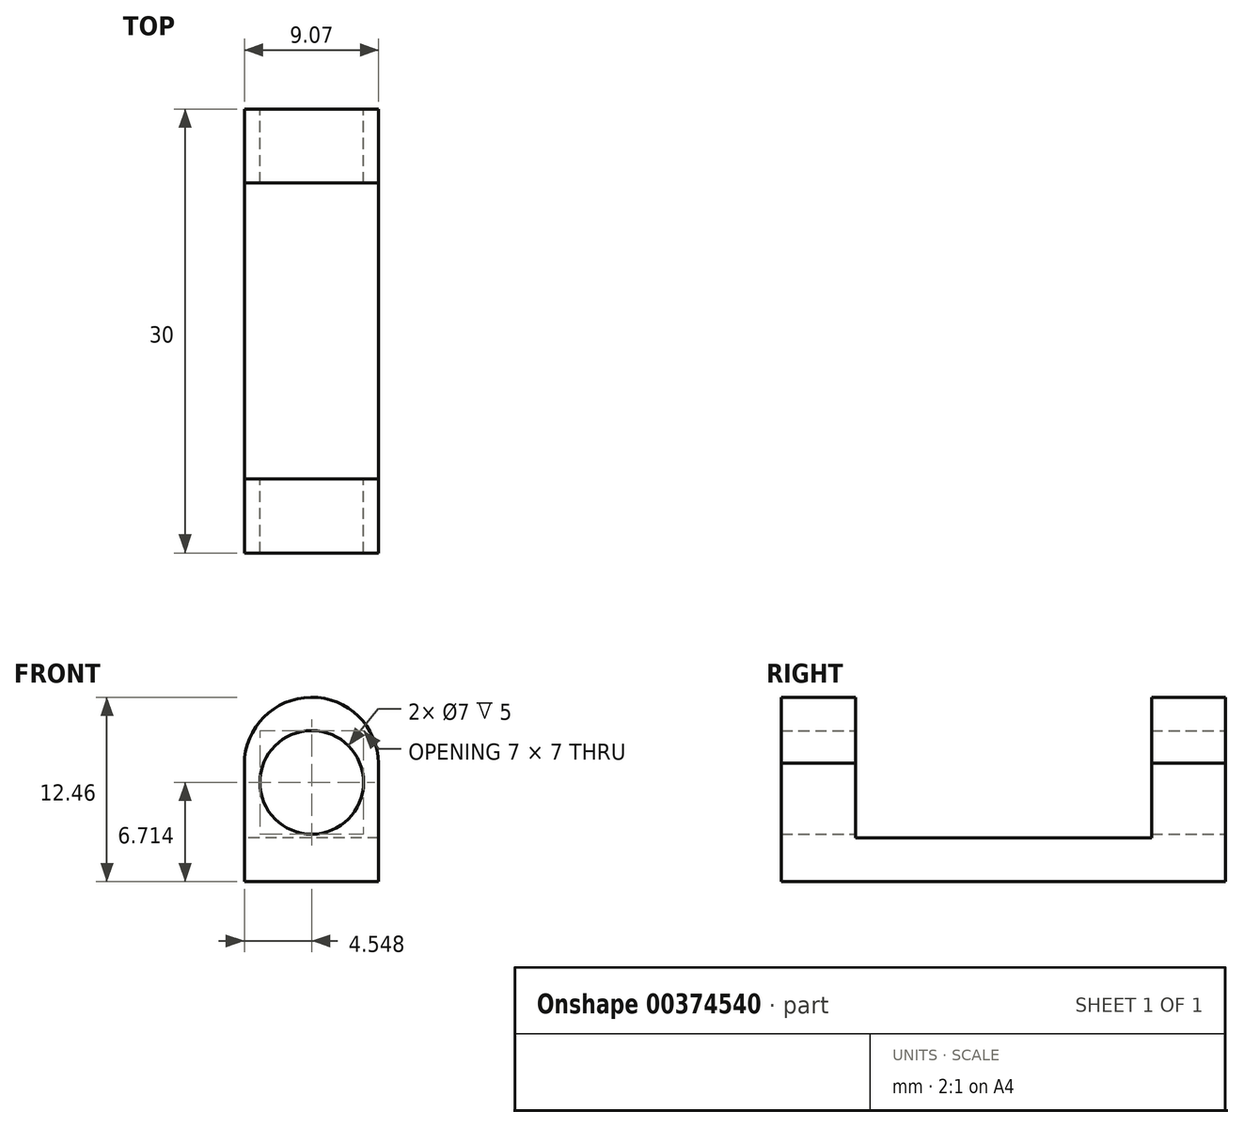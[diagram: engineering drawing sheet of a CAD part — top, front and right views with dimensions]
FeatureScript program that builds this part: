
annotation { "Feature Type Name" : "Feature", "Feature Type Description" : "" }
export const myFeature = defineFeature(function(context is Context, id is Id, definition is map)
    precondition{}
    {
        {
            var Q0;
            Q0=qCreatedBy(makeId("Front.planeOp"),FACE);
            var sketch = newSketch(context, id + "F0", { "sketchPlane" : qUnion([Q0])});
            skLineSegment(sketch, "E0", {"start": v(0, 0) * mm, "end": v(9.07, 0) * mm});
            skLineSegment(sketch, "E1", {"start": v(9.07, 0) * mm, "end": v(9.07, 8) * mm});
            skLineSegment(sketch, "E2", {"start": v(0, 0) * mm, "end": v(0, 7.93) * mm});
            skArc(sketch, "E3", {"start": v(9.07, 8) * mm, "mid": v(4.5, 12.46) * mm, "end": v(0, 7.93) * mm});
            skSolve(sketch);
        }
        {
            var Q0;
            Q0 = qSketchRegion(id + "F0", true);
            extrude(context, id + "F1", {"entities" : qUnion([Q0]), "depth" : 30 * mm});
        }
        {
            var Q0;
            Q0=qCreatedBy(makeId("Front.planeOp"),FACE);
            var sketch = newSketch(context, id + "F2", { "sketchPlane" : qUnion([Q0])});
            skCircle(sketch, "E4", {"center": v(4.55, 6.71) * mm, "radius": 3.5 * mm});
            skSolve(sketch);
        }
        {
            var Q0;
            Q0 = qSketchRegion(id + "F2", true);
            extrude(context, id + "F3", {"entities" : qUnion([Q0]), "operationType" : NewBodyOperationType.REMOVE, "endBound" : BoundingType.THROUGH_ALL, "depth" : 25 * mm});
        }
        {
            var Q0;
            Q0=qCreatedBy(makeId("Right.planeOp"),FACE);
            var sketch = newSketch(context, id + "F4", { "sketchPlane" : qUnion([Q0])});
            skLineSegment(sketch, "E5.bottom", {"start": v(-25, 13) * mm, "end": v(-5, 13) * mm});
            skLineSegment(sketch, "E5.top", {"start": v(-25, 2.97) * mm, "end": v(-5, 2.97) * mm});
            skLineSegment(sketch, "E5.left", {"start": v(-25, 13) * mm, "end": v(-25, 2.97) * mm});
            skLineSegment(sketch, "E5.right", {"start": v(-5, 13) * mm, "end": v(-5, 2.97) * mm});
            skSolve(sketch);
        }
        {
            var Q0;
            Q0=makeQuery(id+"F4.imprint","IMPRINT",FACE,{"disambiguationData":[TD([[makeQuery(id+"F4.imprint","IMPRINT",EDGE,{"derivedFrom":sQuery(id+"F4.wireOp",EDGE,"E5.bottom")}),-1.0]])]});
            extrude(context, id + "F5", {"entities" : qUnion([Q0]), "operationType" : NewBodyOperationType.REMOVE, "endBound" : BoundingType.THROUGH_ALL, "depth" : 25 * mm});
        }
    });
